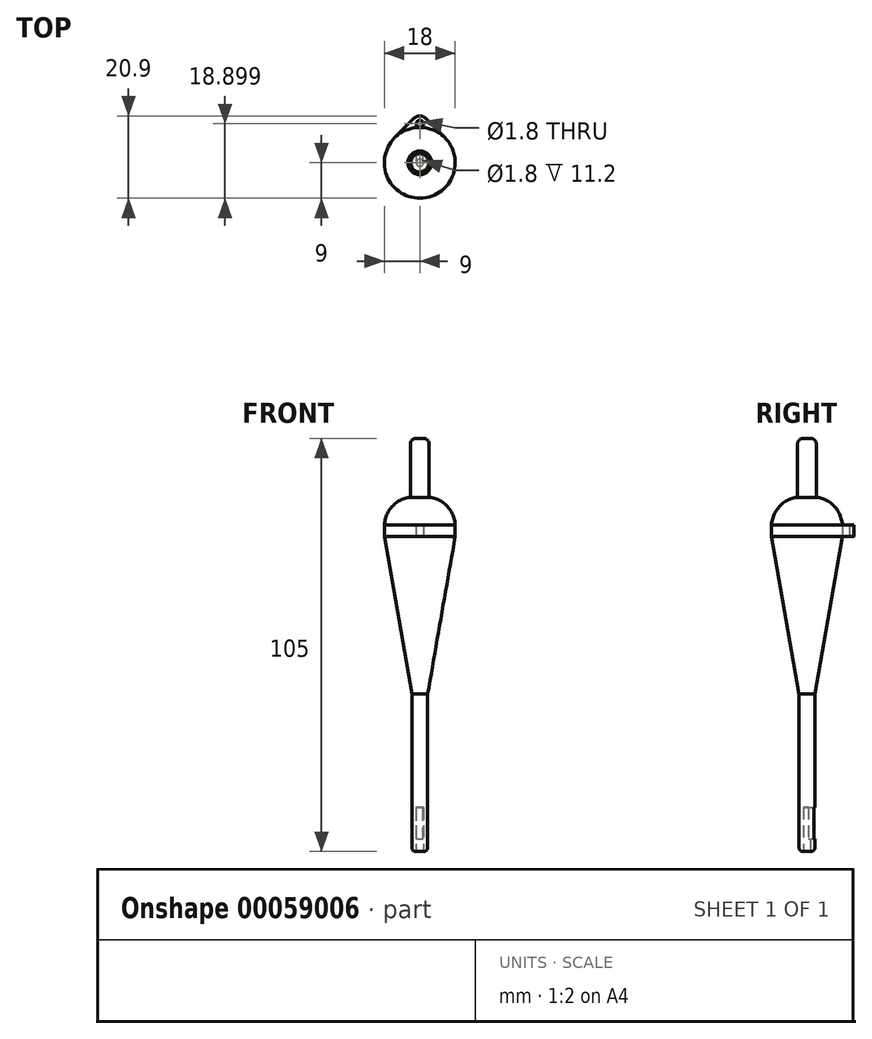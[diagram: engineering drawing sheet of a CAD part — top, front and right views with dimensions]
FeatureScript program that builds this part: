
annotation { "Feature Type Name" : "Feature", "Feature Type Description" : "" }
export const myFeature = defineFeature(function(context is Context, id is Id, definition is map)
    precondition{}
    {
        {
            var Q0;
            Q0=qCreatedBy(makeId("Top.planeOp"),FACE);
            var sketch = newSketch(context, id + "F0", { "sketchPlane" : qUnion([Q0])});
            skArc(sketch, "E0", {"start": v(-6.36, 6.36) * mm, "mid": v(0, -9) * mm, "end": v(6.36, 6.36) * mm});
            skLineSegment(sketch, "E1", {"start": v(-6.36, 6.36) * mm, "end": v(-1.41, 11.31) * mm});
            skLineSegment(sketch, "E2", {"start": v(1.41, 11.31) * mm, "end": v(6.36, 6.36) * mm});
            skPoint(sketch, "E3.visualSharp", {"position": v(0, 12.73) * mm});
            skArc(sketch, "E3.filletArc", {"start": v(1.41, 11.31) * mm, "mid": v(0, 11.9) * mm, "end": v(-1.41, 11.31) * mm});
            skLineSegment(sketch, "E4", {"start": v(0, 0) * mm, "end": v(10.96, 10.96) * mm, "construction": true});
            skCircle(sketch, "E5", {"center": v(0, 0) * mm, "radius": 9 * mm, "construction": true});
            skCircle(sketch, "E6", {"center": v(0, 9.9) * mm, "radius": 0.9 * mm});
            skSolve(sketch);
        }
        {
            var Q0;
            Q0=qSketchRegion(id+"F0",true);
            extrude(context, id + "F1", {"entities" : qUnion([Q0]), "depth" : 3 * mm});
        }
        {
            var Q0;
            Q0=qCreatedBy(makeId("Right.planeOp"),FACE);
            var sketch = newSketch(context, id + "F2", { "sketchPlane" : qUnion([Q0])});
            skLineSegment(sketch, "E7", {"start": v(0, 3) * mm, "end": v(0, 10) * mm});
            skLineSegment(sketch, "E8", {"start": v(0, 10) * mm, "end": v(3, 10) * mm});
            skLineSegment(sketch, "E9", {"start": v(0, 3) * mm, "end": v(9, 3) * mm});
            skArc(sketch, "E10", {"start": v(9, 3) * mm, "mid": v(7.16, 7.5) * mm, "end": v(3, 10) * mm});
            skLineSegment(sketch, "E11", {"start": v(0, 0) * mm, "end": v(0, -80) * mm});
            skLineSegment(sketch, "E12", {"start": v(0, -80) * mm, "end": v(1, -80) * mm});
            skLineSegment(sketch, "E13", {"start": v(2, -79) * mm, "end": v(2, -40) * mm});
            skLineSegment(sketch, "E14", {"start": v(2, -40) * mm, "end": v(9, 0) * mm});
            skLineSegment(sketch, "E15", {"start": v(9, 0) * mm, "end": v(0, 0) * mm});
            skPoint(sketch, "E16.visualSharp", {"position": v(2, -80) * mm});
            skArc(sketch, "E16.filletArc", {"start": v(1, -80) * mm, "mid": v(1.7, -79.7) * mm, "end": v(2, -79) * mm});
            skSolve(sketch);
        }
        {
            var Q0;
            Q0=qSketchRegion(id+"F2",true);
            var Q1;
            Q1=sQuery(id+"F2.wireOp",EDGE,"E11");
            revolve(context, id + "F3", {"operationType" : NewBodyOperationType.ADD, "entities" : qUnion([Q0]), "axis" : qUnion([Q1]), "revolveType" : RevolveType.FULL});
        }
        {
            var Q0;
            Q0=qCreatedBy(makeId("Front.planeOp"),FACE);
            cPlane(context, id + "F4", {"entities" : qUnion([Q0]), "cplaneType" : CPlaneType.OFFSET, "offset" : 9 * mm, "oppositeDirection" : true, "width" : 150 * mm, "height" : 150 * mm});
        }
        {
            var Q0;
            Q0=qCreatedBy(id+"F4.planeOp",FACE);
            var sketch = newSketch(context, id + "F5", { "sketchPlane" : qUnion([Q0])});
            skLineSegment(sketch, "E17", {"start": v(0, 0) * mm, "end": v(0, -61.52) * mm, "construction": true});
            skLineSegment(sketch, "E18.bottom", {"start": v(0.8, -76.8) * mm, "end": v(-0.8, -76.8) * mm});
            skLineSegment(sketch, "E18.top", {"start": v(0.8, -68.8) * mm, "end": v(-0.8, -68.8) * mm});
            skLineSegment(sketch, "E18.left", {"start": v(0.8, -76.8) * mm, "end": v(0.8, -68.8) * mm});
            skLineSegment(sketch, "E18.right", {"start": v(-0.8, -76.8) * mm, "end": v(-0.8, -68.8) * mm});
            skSolve(sketch);
        }
        {
            var Q0;
            Q0=qSketchRegion(id+"F5",true);
            extrude(context, id + "F6", {"entities" : qUnion([Q0]), "operationType" : NewBodyOperationType.REMOVE, "depth" : 9 * mm});
        }
        {
            var Q0;
            Q0=makeQuery(id+"F3.opRevolve","SWEPT_FACE",FACE,{"disambiguationData":[OSD([sQuery(id+"F2.wireOp",EDGE,"E12")])]});
            var sketch = newSketch(context, id + "F7", { "sketchPlane" : qUnion([Q0])});
            skCircle(sketch, "E19", {"center": v(0, 0) * mm, "radius": 0.9 * mm});
            skSolve(sketch);
        }
        {
            var Q0;
            Q0=qSketchRegion(id+"F7",true);
            extrude(context, id + "F8", {"entities" : qUnion([Q0]), "operationType" : NewBodyOperationType.REMOVE, "oppositeDirection" : true, "depth" : 11.2 * mm});
        }
        {
            var Q0;
            Q0=makeQuery(id+"F3.opRevolve","SWEPT_FACE",FACE,{"disambiguationData":[OSD([sQuery(id+"F2.wireOp",EDGE,"E8")])]});
            var sketch = newSketch(context, id + "F9", { "sketchPlane" : qUnion([Q0])});
            skCircle(sketch, "E20", {"center": v(0, 0) * mm, "radius": 2.4 * mm});
            skSolve(sketch);
        }
        {
            var Q0;
            Q0=qSketchRegion(id+"F9",true);
            extrude(context, id + "F10", {"entities" : qUnion([Q0]), "operationType" : NewBodyOperationType.ADD, "depth" : 15 * mm});
        }
        {
            var Q0;
            Q0=makeQuery(id+"F10.opExtrude","CAP_EDGE",EDGE,{"disambiguationData":[OSD([sQuery(id+"F9.wireOp",EDGE,"E20")])],"isStart":false});
            fillet(context, id + "F11", {"entities" : qUnion([Q0]), "radius" : 1.5 * mm, "allowEdgeOverflow" : false});
        }
    });
